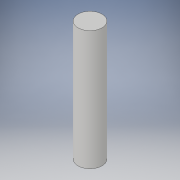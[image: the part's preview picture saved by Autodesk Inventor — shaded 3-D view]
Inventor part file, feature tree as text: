
AUTODESK INVENTOR PART (.ipt)
format: ipt  version: 2018 (Build 220112000, 112)  size: 88,064 bytes
history: native  units: in
note: dims shown in document units (in); Inventor stores cm internally (conversion verified against a paired STEP export)
features: extrude x1, sketch x1
ambient origin geometry x8: Origin, YZ Plane, XZ Plane, XY Plane, X Axis, Y Axis, Z Axis, Center Point
bodies: Solid1 (feature_tree)
feature tree (2):
  extrude  "Extrusion1"  Depth=5.0in TaperAngle=0.0deg
  sketch  "Sketch1"  dims[d0=1.0in d1=5.0in d2=0.0in]
